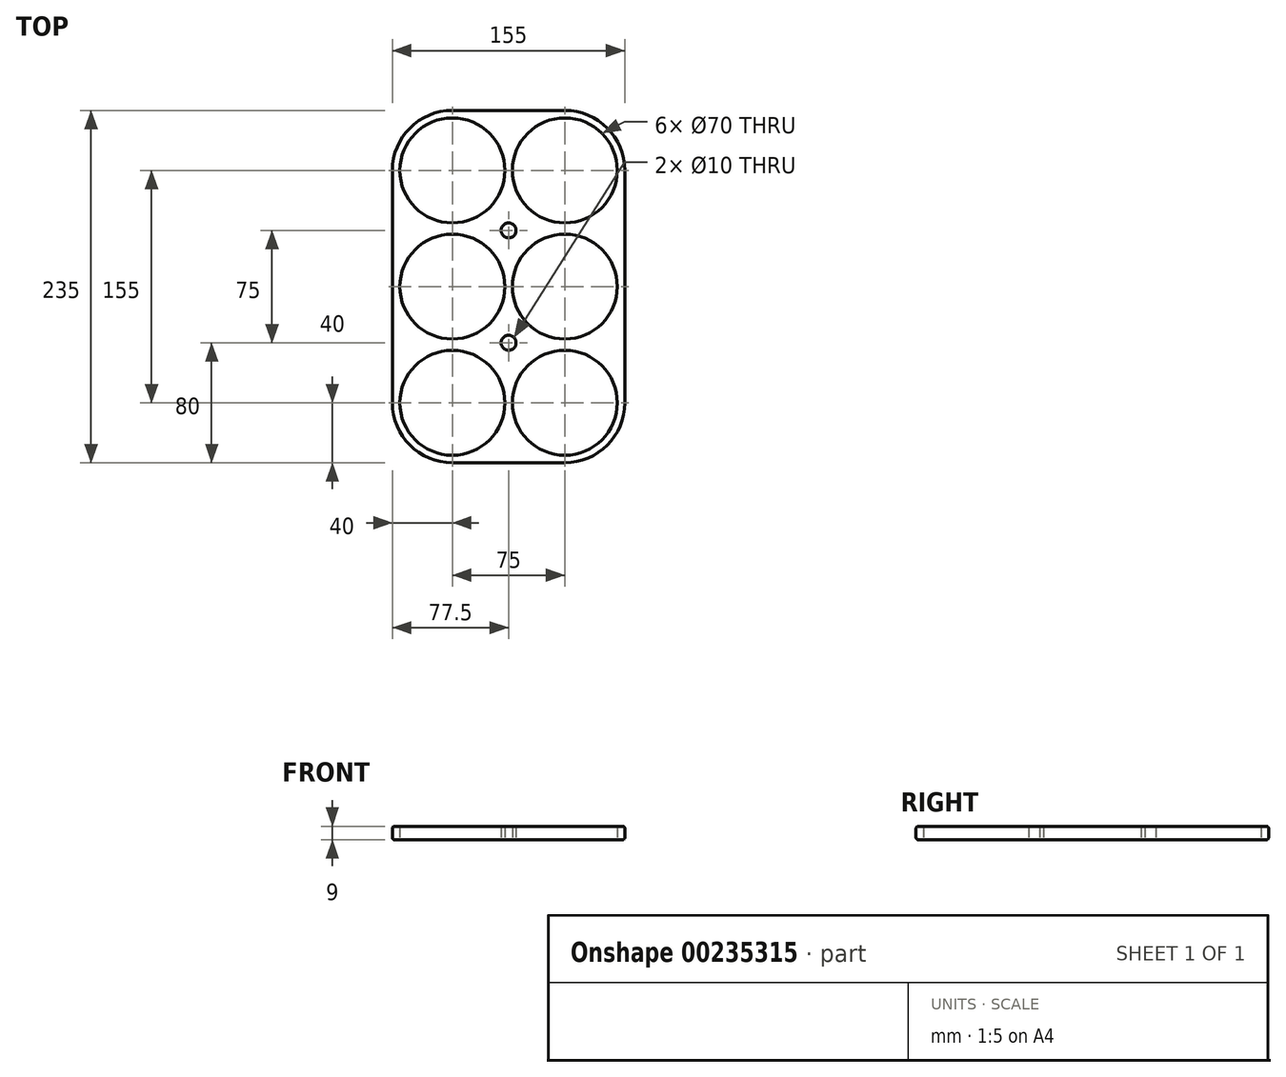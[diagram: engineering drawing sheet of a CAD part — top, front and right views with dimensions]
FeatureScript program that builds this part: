
annotation { "Feature Type Name" : "Feature", "Feature Type Description" : "" }
export const myFeature = defineFeature(function(context is Context, id is Id, definition is map)
    precondition{}
    {
        {
            var Q0;
            Q0=qCreatedBy(makeId("Top.planeOp"),FACE);
            var sketch = newSketch(context, id + "F0", { "sketchPlane" : qUnion([Q0])});
            skLineSegment(sketch, "E0.bottom", {"start": v(40, 0) * mm, "end": v(115, 0) * mm});
            skLineSegment(sketch, "E0.top", {"start": v(40, 235) * mm, "end": v(115, 235) * mm});
            skLineSegment(sketch, "E0.left", {"start": v(0, 40) * mm, "end": v(0, 195) * mm});
            skLineSegment(sketch, "E0.right", {"start": v(155, 40) * mm, "end": v(155, 195) * mm});
            skPoint(sketch, "E1.visualSharp", {"position": v(0, 235) * mm});
            skArc(sketch, "E1.filletArc", {"start": v(40, 235) * mm, "mid": v(11.72, 223.28) * mm, "end": v(0, 195) * mm});
            skPoint(sketch, "E2.visualSharp", {"position": v(155, 235) * mm});
            skArc(sketch, "E2.filletArc", {"start": v(155, 195) * mm, "mid": v(143.28, 223.28) * mm, "end": v(115, 235) * mm});
            skPoint(sketch, "E3.visualSharp", {"position": v(155, 0) * mm});
            skArc(sketch, "E3.filletArc", {"start": v(115, 0) * mm, "mid": v(143.28, 11.72) * mm, "end": v(155, 40) * mm});
            skPoint(sketch, "E4.visualSharp", {"position": v(0, 0) * mm});
            skArc(sketch, "E4.filletArc", {"start": v(0, 40) * mm, "mid": v(11.72, 11.72) * mm, "end": v(40, 0) * mm});
            skCircle(sketch, "E5", {"center": v(40, 195) * mm, "radius": 35 * mm});
            skCircle(sketch, "E6", {"center": v(115, 195) * mm, "radius": 35 * mm});
            skCircle(sketch, "E7", {"center": v(40, 40) * mm, "radius": 35 * mm});
            skCircle(sketch, "E8", {"center": v(115, 40) * mm, "radius": 35 * mm});
            skCircle(sketch, "E9", {"center": v(40, 117.5) * mm, "radius": 35 * mm});
            skPoint(sketch, "E9.centerSnap0", {"position": v(0, 117.5) * mm});
            skCircle(sketch, "E10", {"center": v(115, 117.5) * mm, "radius": 35 * mm});
            skCircle(sketch, "E11", {"center": v(77.5, 155) * mm, "radius": 5 * mm});
            skPoint(sketch, "E11.centerSnap0", {"position": v(77.5, 235) * mm});
            skCircle(sketch, "E12", {"center": v(77.5, 80) * mm, "radius": 5 * mm});
            skSolve(sketch);
        }
        {
            var Q0;
            Q0=makeQuery(id+"F0.imprint","IMPRINT",FACE,{"disambiguationData":[TD([[makeQuery(id+"F0.imprint","IMPRINT",EDGE,{"derivedFrom":sQuery(id+"F0.wireOp",EDGE,"E0.bottom")}),1.0]])]});
            extrude(context, id + "F1", {"entities" : qUnion([Q0]), "depth" : 9 * mm});
        }
        {
            var Q0;
            Q0=makeQuery(id+"F1.opExtrude","CAP_EDGE",EDGE,{"disambiguationData":[OSD([sQuery(id+"F0.wireOp",EDGE,"E0.left")])],"isStart":false});
            var Q1;
            Q1=makeQuery(id+"F1.opExtrude","CAP_EDGE",EDGE,{"disambiguationData":[OSD([sQuery(id+"F0.wireOp",EDGE,"E0.bottom")])],"isStart":true});
            fillet(context, id + "F2", {"entities" : qUnion([Q0, Q1]), "radius" : 1.5 * mm, "tangentPropagation" : true, "allowEdgeOverflow" : false});
        }
    });
